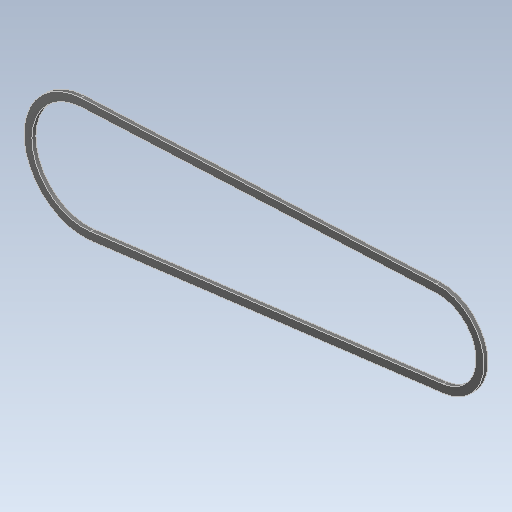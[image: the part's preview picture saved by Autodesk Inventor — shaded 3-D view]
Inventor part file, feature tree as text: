
AUTODESK INVENTOR PART (.ipt)
format: ipt  version: 2021 (Build 250183000, 183)  size: 96,768 bytes
history: mixed  units: mm
features: other x1, extrude x1, imported_body x1
ambient origin geometry x8: Origin, YZ Plane, XZ Plane, XY Plane, X Axis, Y Axis, Z Axis, Center Point
bodies: Body1 (imported_parasolid)
feature tree (3):
  other  "Sólido1"
  extrude  "Extrude-Thin1"  [1 undecoded]
  imported_body  NMx_Import_Brep_tag  [imported B-rep: ~10 faces, bbox_mm=[455.81797, 170.033257, 5.0]]
note: 1 required parameter value undecoded (feature->parameter linkage not recoverable at this tier; creation-order binding heuristic only, values carry confidence <= 0.55)
